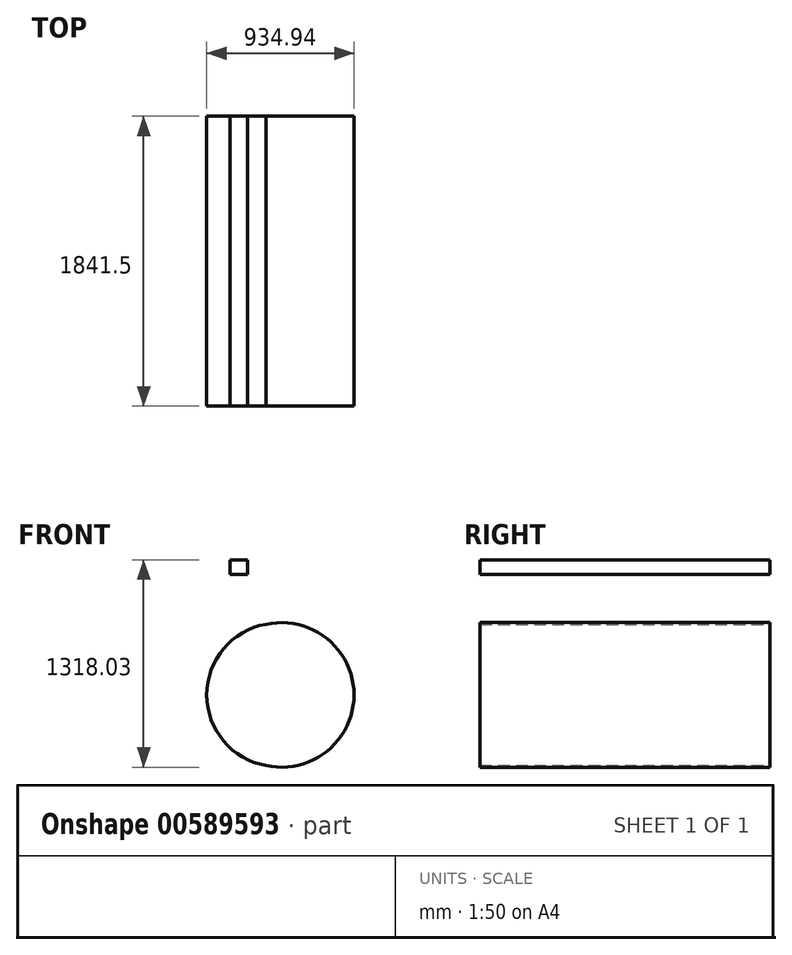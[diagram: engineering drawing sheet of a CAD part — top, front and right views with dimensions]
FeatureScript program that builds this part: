
annotation { "Feature Type Name" : "Feature", "Feature Type Description" : "" }
export const myFeature = defineFeature(function(context is Context, id is Id, definition is map)
    precondition{}
    {
        {
            var Q0;
            Q0=qCreatedBy(makeId("Front.planeOp"),FACE);
            var sketch = newSketch(context, id + "F0", { "sketchPlane" : qUnion([Q0])});
            skLineSegment(sketch, "E0.bottom", {"start": v(-58.42, 44.03) * mm, "end": v(52.08, 44.03) * mm});
            skLineSegment(sketch, "E0.top", {"start": v(-58.42, -49.64) * mm, "end": v(52.08, -49.64) * mm});
            skLineSegment(sketch, "E0.left", {"start": v(-58.42, 44.03) * mm, "end": v(-58.42, -49.64) * mm});
            skLineSegment(sketch, "E0.right", {"start": v(52.08, 44.03) * mm, "end": v(52.08, -49.64) * mm});
            skCircle(sketch, "E1", {"center": v(248.82, -814.65) * mm, "radius": 455.44 * mm});
            skCircle(sketch, "E2", {"center": v(248.82, -814.65) * mm, "radius": 417.7 * mm});
            skCircle(sketch, "E3", {"center": v(268.97, -814.65) * mm, "radius": 459.35 * mm});
            skSolve(sketch);
        }
        {
            var Q0;
            Q0=makeQuery(id+"F0.imprint","IMPRINT",FACE,{"disambiguationData":[TD([[makeQuery(id+"F0.imprint","IMPRINT",EDGE,{"derivedFrom":sQuery(id+"F0.wireOp",EDGE,"E0.bottom")}),-1.0]])]});
            var Q1;
            {var subQ0=sQuery(id+"F0.wireOp",EDGE,"E3");var subQ1=sQuery(id+"F0.wireOp",EDGE,"E1");var subQ2=makeQuery(id+"F0.imprint","INTERSECT",VERTEX,{"disambiguationData":[OD(0.0)],"derivedFrom":[subQ1,subQ0]});Q1=makeQuery(id+"F0.imprint","IMPRINT",FACE,{"disambiguationData":[TD([[makeQuery(id+"F0.imprint","IMPRINT",EDGE,{"disambiguationData":[TD([[subQ2,1.0]])],"derivedFrom":subQ1}),1.0]])]});}
            var Q2;
            {var subQ0=sQuery(id+"F0.wireOp",EDGE,"E3");var subQ1=sQuery(id+"F0.wireOp",EDGE,"E1");var subQ2=makeQuery(id+"F0.imprint","INTERSECT",VERTEX,{"disambiguationData":[OD(0.0)],"derivedFrom":[subQ1,subQ0]});Q2=makeQuery(id+"F0.imprint","IMPRINT",FACE,{"disambiguationData":[TD([[makeQuery(id+"F0.imprint","IMPRINT",EDGE,{"disambiguationData":[TD([[subQ2,-1.0]])],"derivedFrom":subQ1}),-1.0]])]});}
            var Q3;
            Q3=makeQuery(id+"F0.imprint","IMPRINT",FACE,{"disambiguationData":[TD([[makeQuery(id+"F0.imprint","IMPRINT",EDGE,{"derivedFrom":sQuery(id+"F0.wireOp",EDGE,"E2")}),-1.0]])]});
            var Q4;
            Q4=makeQuery(id+"F0.imprint","IMPRINT",FACE,{"disambiguationData":[TD([[makeQuery(id+"F0.imprint","IMPRINT",EDGE,{"derivedFrom":sQuery(id+"F0.wireOp",EDGE,"E2")}),1.0]])]});
            extrude(context, id + "F1", {"entities" : qUnion([Q0, Q1, Q2, Q3, Q4]), "depth" : 1841.5 * mm, "offsetDistance" : 25.4 * mm});
        }
    });
